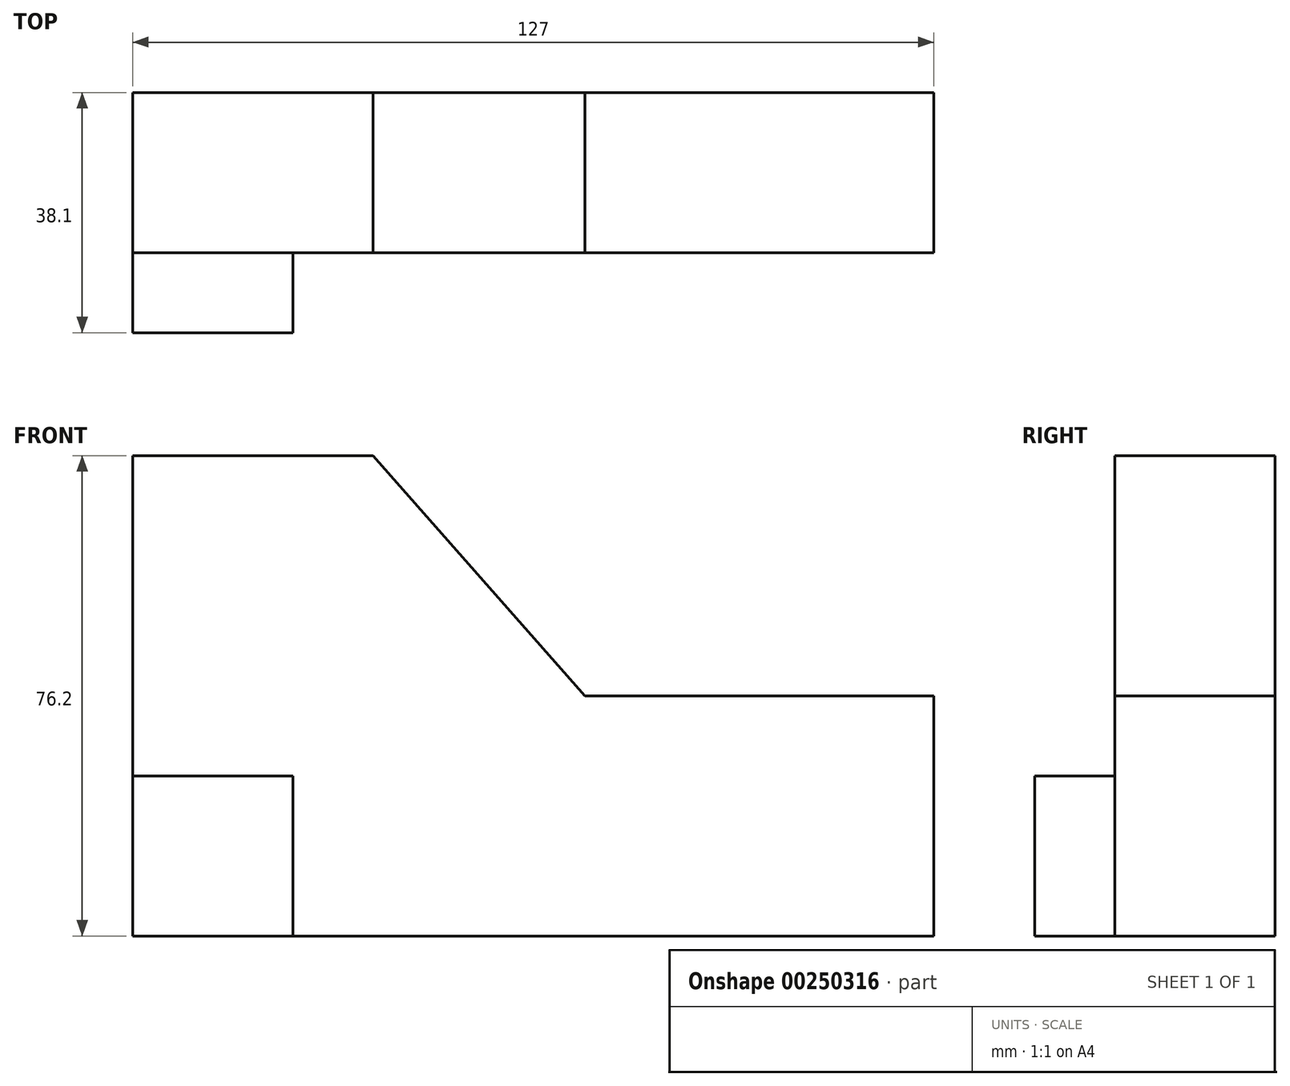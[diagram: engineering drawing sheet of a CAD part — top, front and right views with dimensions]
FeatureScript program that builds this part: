
annotation { "Feature Type Name" : "Feature", "Feature Type Description" : "" }
export const myFeature = defineFeature(function(context is Context, id is Id, definition is map)
    precondition{}
    {
        {
            var Q0;
            Q0=qCreatedBy(makeId("Front.planeOp"),FACE);
            var sketch = newSketch(context, id + "F0", { "sketchPlane" : qUnion([Q0])});
            skLineSegment(sketch, "E0", {"start": v(0, 0) * mm, "end": v(127, 0) * mm});
            skLineSegment(sketch, "E1", {"start": v(127, 0) * mm, "end": v(127, 38.1) * mm});
            skLineSegment(sketch, "E2", {"start": v(127, 38.1) * mm, "end": v(0, 38.1) * mm});
            skLineSegment(sketch, "E3", {"start": v(0, 38.1) * mm, "end": v(0, 25.4) * mm});
            skLineSegment(sketch, "E4", {"start": v(0, 38.1) * mm, "end": v(0, 76.2) * mm});
            skLineSegment(sketch, "E5", {"start": v(0, 76.2) * mm, "end": v(38.1, 76.2) * mm});
            skLineSegment(sketch, "E6", {"start": v(38.1, 76.2) * mm, "end": v(71.7, 38.1) * mm});
            skPoint(sketch, "E7.start.orphan", {"position": v(0, 25.4) * mm});
            skLineSegment(sketch, "E8", {"start": v(0, 38.1) * mm, "end": v(0, 0) * mm});
            skSolve(sketch);
        }
        {
            var Q0;
            {var subQ0=sQuery(id+"F0.wireOp",EDGE,"E4");Q0=makeQuery(id+"F0.imprint","IMPRINT",FACE,{"disambiguationData":[TD([[makeQuery(id+"F0.imprint","IMPRINT",EDGE,{"derivedFrom":subQ0}),-1.0]])]});}
            var Q1;
            {var subQ5=sQuery(id+"F0.wireOp",EDGE,"E0");Q1=makeQuery(id+"F0.imprint","IMPRINT",FACE,{"disambiguationData":[TD([[makeQuery(id+"F0.imprint","IMPRINT",EDGE,{"derivedFrom":subQ5}),1.0]])]});}
            extrude(context, id + "F1", {"entities" : qUnion([Q0, Q1]), "depth" : 25.4 * mm});
        }
        {
            var Q0;
            Q0=makeQuery(id+"F1.opExtrude","CAP_FACE",FACE,{"disambiguationData":[OSD([sQuery(id+"F0.wireOp",EDGE,"E0"),sQuery(id+"F0.wireOp",EDGE,"E1"),sQuery(id+"F0.wireOp",EDGE,"E2"),sQuery(id+"F0.wireOp",EDGE,"E4"),sQuery(id+"F0.wireOp",EDGE,"E5"),sQuery(id+"F0.wireOp",EDGE,"E6"),sQuery(id+"F0.wireOp",EDGE,"E8")])],"isStart":false});
            var sketch = newSketch(context, id + "F2", { "sketchPlane" : qUnion([Q0])});
            skLineSegment(sketch, "E9", {"start": v(0, 0) * mm, "end": v(25.4, 0) * mm});
            skLineSegment(sketch, "E10", {"start": v(25.4, 0) * mm, "end": v(25.4, 25.4) * mm});
            skLineSegment(sketch, "E11", {"start": v(25.4, 25.4) * mm, "end": v(0, 25.4) * mm});
            skLineSegment(sketch, "E12", {"start": v(0, 25.4) * mm, "end": v(0, 0) * mm});
            skSolve(sketch);
        }
        {
            var Q0;
            Q0=makeQuery(id+"F2.imprint","IMPRINT",FACE,{"disambiguationData":[TD([[makeQuery(id+"F2.imprint","IMPRINT",EDGE,{"derivedFrom":sQuery(id+"F2.wireOp",EDGE,"E9")}),1.0]])]});
            extrude(context, id + "F3", {"entities" : qUnion([Q0]), "operationType" : NewBodyOperationType.ADD, "depth" : 12.7 * mm});
        }
    });
